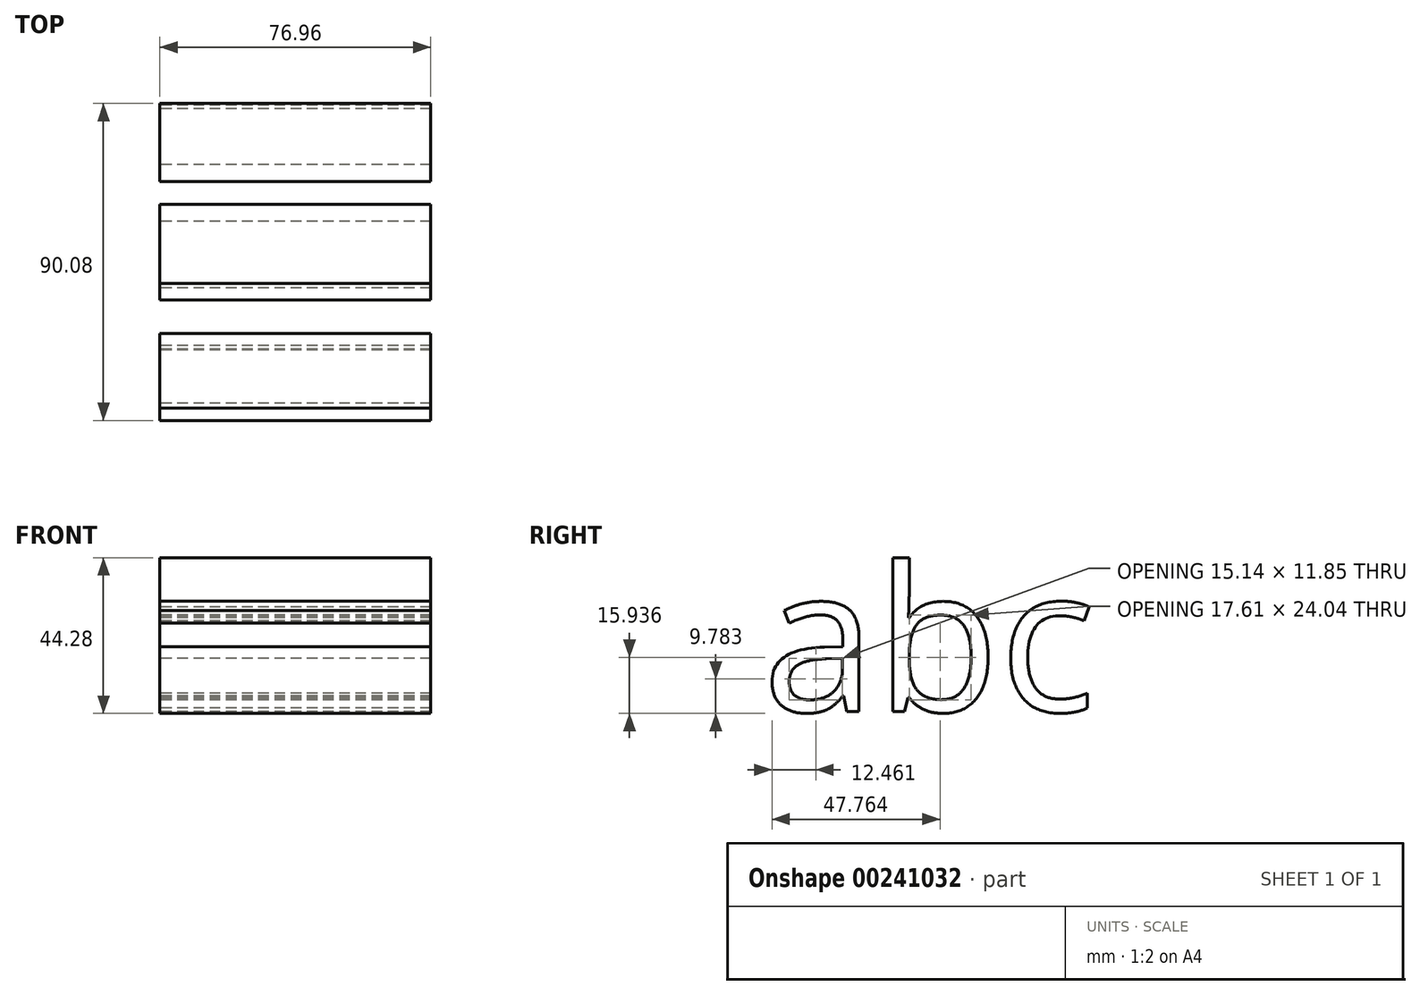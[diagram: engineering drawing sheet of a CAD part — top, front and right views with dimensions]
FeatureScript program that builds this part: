
annotation { "Feature Type Name" : "Feature", "Feature Type Description" : "" }
export const myFeature = defineFeature(function(context is Context, id is Id, definition is map)
    precondition{}
    {
        {
            var Q0;
            Q0=qCreatedBy(makeId("Right.planeOp"),FACE);
            var sketch = newSketch(context, id + "F0", { "sketchPlane" : qUnion([Q0])});
            skText(sketch, "E0", { "text": "abc", "fontName": "OpenSans-Regular.ttf"});
            const initialGuessF0  = {"E0": [-0.03545, -0.02895, 1, 0, 0.04142]};
            skSetInitialGuess(sketch, initialGuessF0);
            skSolve(sketch);
        }
        {
            var Q0;
            Q0 = qSketchRegion(id + "F0", true);
            extrude(context, id + "F1", {"entities" : qUnion([Q0]), "depth" : 76.96 * mm});
        }
    });
